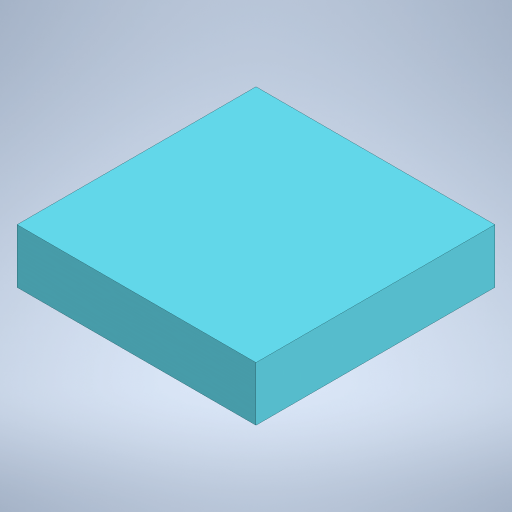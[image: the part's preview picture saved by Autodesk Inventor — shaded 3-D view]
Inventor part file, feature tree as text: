
AUTODESK INVENTOR PART (.ipt)
format: ipt  version: 2024 (Build 280153000, 153)  size: 5,346,816 bytes
history: native  units: mm
features: other x26, surface_op x18, fillet x9, sketch x9, extrude x6, revolve x4, plane x3, pattern_circular x2, loft x1
ambient origin geometry x8: Origin, YZ Plane, XZ Plane, XY Plane, X Axis, Y Axis, Z Axis, Center Point
bodies: Body1 (feature_tree), Body2 (feature_tree), Body3 (feature_tree), Body4 (feature_tree), Body5 (feature_tree), Body6 (feature_tree), Body7 (feature_tree), Body8 (feature_tree), Body9 (feature_tree), Body10 (feature_tree), Body11 (feature_tree), Body12 (feature_tree), Body13 (feature_tree), Body14 (feature_tree), Body15 (feature_tree), Body16 (feature_tree), Body17 (feature_tree), Body18 (feature_tree), Body19 (feature_tree), Body20 (feature_tree), Body21 (feature_tree), Body22 (feature_tree), Body23 (feature_tree), Body24 (feature_tree), Body25 (feature_tree), Body26 (feature_tree), Body27 (feature_tree)
feature tree (78):
  plane  "Work Plane1"
  plane  "Work Plane4"
  plane  "Work Plane5"
  surface_op  "Trim1"
  surface_op  "Trim2"
  surface_op  "Trim3"
  surface_op  "Trim4"
  fillet  "Fillet1"  Radius=200.0mm
  pattern_circular  "Circular Pattern1"  Count=11  [1 undecoded]
  surface_op  "Stitch Surface2"
  pattern_circular  "Circular Pattern3"  Count=3  [1 undecoded]
  surface_op  "Trim7"
  surface_op  "Trim8"
  surface_op  "Trim9"
  surface_op  "Trim10"
  surface_op  "Trim11"
  surface_op  "Stitch Surface3"
  extrude  "Extrusion4"  Depth=200.0mm
  surface_op  "Sculpt2"
  sketch  "Sketch1"  dims[d2=463.0mm]
  other  "Srf1"
  sketch  "Sketch2"  dims[d3=138.0mm]
  other  "Srf2"
  sketch  "Sketch3"  dims[d4=95.0mm]
  other  "Srf3"
  sketch  "Sketch4"  dims[d5=84.0mm]
  sketch  "Sketch7"  dims[d6=33.0mm]
  sketch  "Sketch8"  dims[d7=12.566371mm d8=30.0mm]
  other  "Srf4"
  other  "Srf5"
  other  "Srf6"
  sketch  "Sketch9"  dims[d9=35.0mm d10=200.0mm]
  other  "Srf7"
  other  "Srf8"
  other  "Srf9"
  other  "Srf10"
  other  "Srf11"
  other  "Srf12"
  other  "Srf13"
  other  "Srf15"
  sketch  "Sketch11"  dims[d11=12.566371mm d12=369.0mm]
  other  "Srf18"
  other  "Srf19"
  other  "Srf20"
  other  "Srf21"
  other  "Srf22"
  other  "Srf23"
  other  "Srf24"
  other  "Srf25"
  other  "Srf26"
  other  "Srf27"
  other  "Srf29"
  other  "Srf30"
  sketch  "Sketch13"  dims[d13=50.0mm d14=245.0mm d15=16.0mm d16=130.0mm d17=63.0mm d18=12.566371mm d19=120.0mm d21=-25.0mm d22=-120.0mm d27=100.0mm d28=152.0mm d29=80.0mm d30=45.0mm d31=6.283185mm d32=6.283185mm d33=360.0mm d36=25.0mm d37=50.0mm d38=0.0mm d39=90.0deg d40=0.0mm d41=90.0deg d42=0.0mm d43=90.0deg d44=15.0mm d45=25.0mm d46=30.0mm d47=30.0mm d48=70.0mm d49=80.0mm d50=20.0mm d51=75.0mm d52=12.566371mm d53=5.0mm d54=5.0mm d55=5.0mm d56=5.0mm d57=5.0mm d58=5.0mm d59=5.0mm d60=5.0mm d61=50.0mm d62=360.0deg d68=80.0mm d69=300.0mm d79=10.0mm d80=0.0mm d81=50.0mm d82=360.0deg d84=5.0mm d85=0.0mm d86=5.0mm d87=0.0mm d88=5.0mm d89=0.0mm d90=5.0mm d91=0.0mm d92=5.0mm d93=0.0mm d102=5.0mm d103=0.0mm d104=1100.0mm d105=550.0mm d106=250.0mm d107=68.0mm d108=1100.0mm d109=0.0mm]
  revolve  "RevolutionSrf1"  [1 undecoded]
  revolve  "RevolutionSrf2"  [1 undecoded]
  revolve  "RevolutionSrf3"  [1 undecoded]
  loft  "LoftSrf1"
  fillet  "Face Fillet2"
  revolve  "RevolutionSrf4"  [1 undecoded]
  fillet  "Face Fillet4"
  extrude  "ExtrusionSrf3"  Depth=12.566371mm
  fillet  "Face Fillet1"
  fillet  "Face Fillet3"
  fillet  "Face Fillet5"
  fillet  "Face Fillet6"
  fillet  "Face Fillet7"
  fillet  "Face Fillet8"
  extrude  "ExtrusionSrf4"  Depth=120.0mm
  extrude  "ExtrusionSrf5"  Depth=100.0mm
  extrude  "ExtrusionSrf6"  Depth=152.0mm
  extrude  "ExtrusionSrf7"  Depth=80.0mm
  surface_op  "Boundary Patch1"
  surface_op  "Boundary Patch2"
  surface_op  "Boundary Patch3"
  surface_op  "Boundary Patch4"
  surface_op  "Boundary Patch5"
  surface_op  "Boundary Patch7"
note: 6 required parameter values undecoded (feature->parameter linkage not recoverable at this tier; creation-order binding heuristic only, values carry confidence <= 0.55)